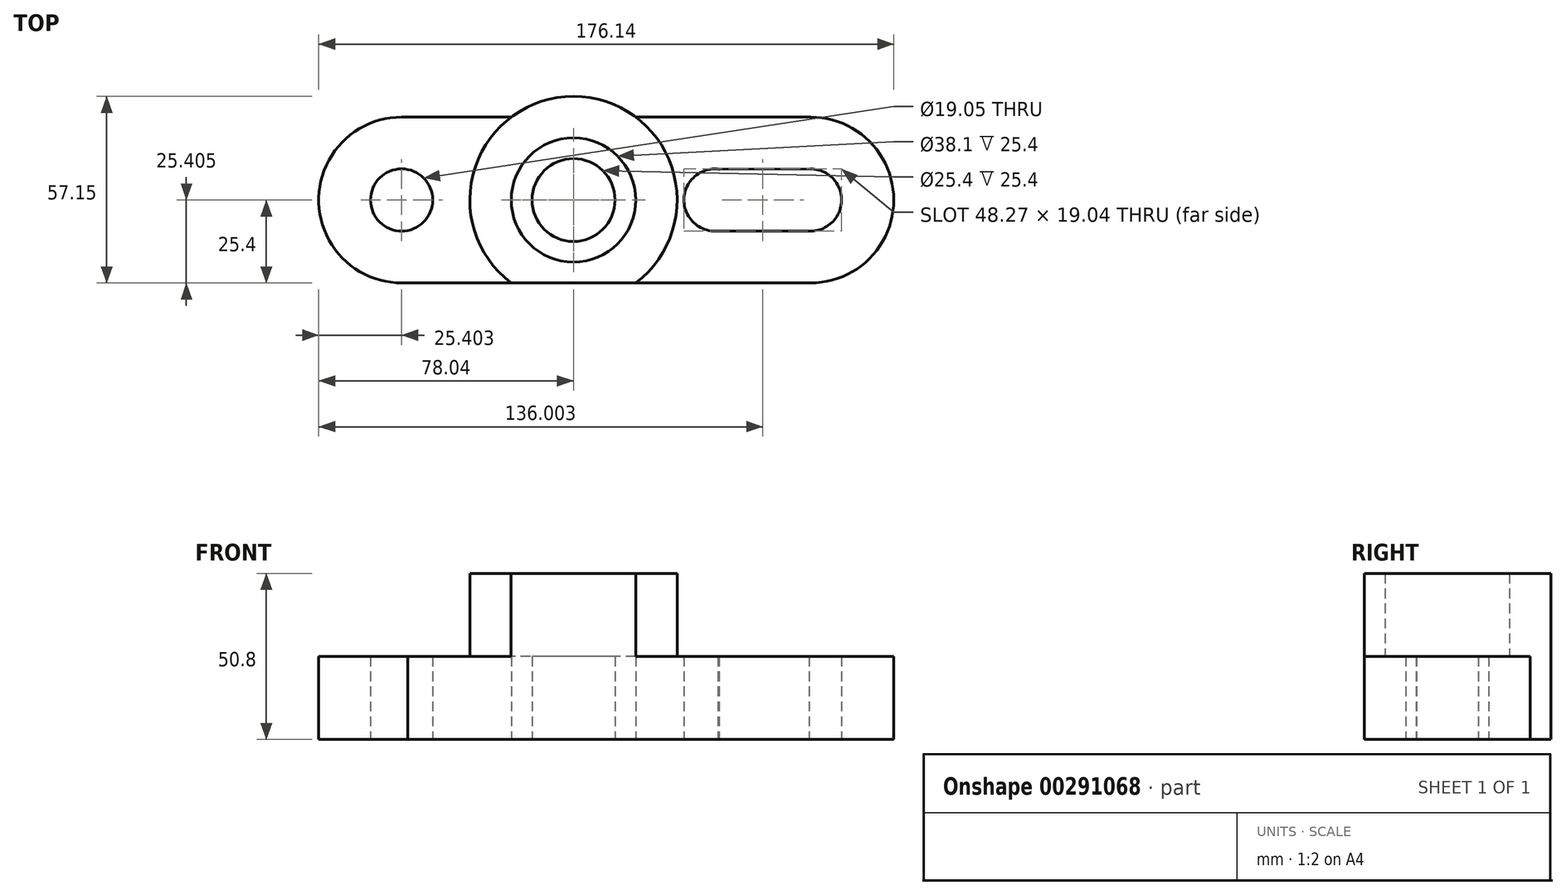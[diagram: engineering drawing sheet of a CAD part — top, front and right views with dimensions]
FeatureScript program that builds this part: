
annotation { "Feature Type Name" : "Feature", "Feature Type Description" : "" }
export const myFeature = defineFeature(function(context is Context, id is Id, definition is map)
    precondition{}
    {
        {
            var Q0;
            Q0=qCreatedBy(makeId("Top.planeOp"),FACE);
            var sketch = newSketch(context, id + "F0", { "sketchPlane" : qUnion([Q0])});
            skCircle(sketch, "E0", {"center": v(0, 0) * mm, "radius": 12.7 * mm});
            skCircle(sketch, "E1", {"center": v(0, 0) * mm, "radius": 19.05 * mm});
            skCircle(sketch, "E2", {"center": v(0, 0) * mm, "radius": 31.75 * mm});
            skArc(sketch, "E3", {"start": v(-52.64, 25.4) * mm, "mid": v(-78.02, -0.9) * mm, "end": v(-50.82, -25.33) * mm});
            skArc(sketch, "E4", {"start": v(72.69, -25.4) * mm, "mid": v(98.1, 0) * mm, "end": v(72.7, 25.4) * mm});
            skLineSegment(sketch, "E5", {"start": v(-54.48, -25.33) * mm, "end": v(72.69, -25.4) * mm});
            skLineSegment(sketch, "E6", {"start": v(72.7, 25.4) * mm, "end": v(-52.64, 25.4) * mm});
            skCircle(sketch, "E7", {"center": v(-52.64, 0) * mm, "radius": 9.53 * mm});
            skCircle(sketch, "E8", {"center": v(43.35, 0) * mm, "radius": 9.53 * mm});
            skCircle(sketch, "E9", {"center": v(72.57, 0) * mm, "radius": 9.53 * mm});
            skLineSegment(sketch, "E10", {"start": v(44.6, 9.44) * mm, "end": v(72.54, 9.52) * mm});
            skLineSegment(sketch, "E11", {"start": v(44.18, -9.49) * mm, "end": v(72.12, -9.51) * mm});
            skSolve(sketch);
        }
        {
            var Q0;
            {var subQ0=sQuery(id+"F0.wireOp",EDGE,"E6");var subQ1=sQuery(id+"F0.wireOp",EDGE,"E2");var subQ2=makeQuery(id+"F0.imprint","INTERSECT",VERTEX,{"disambiguationData":[OD(0.0)],"derivedFrom":[subQ1,subQ0]});Q0=makeQuery(id+"F0.imprint","IMPRINT",FACE,{"disambiguationData":[TD([[makeQuery(id+"F0.imprint","IMPRINT",EDGE,{"disambiguationData":[TD([[subQ2,1.0]])],"derivedFrom":subQ1}),1.0]])]});}
            var Q1;
            {var subQ0=sQuery(id+"F0.wireOp",EDGE,"E5");var subQ1=sQuery(id+"F0.wireOp",EDGE,"E2");var subQ2=makeQuery(id+"F0.imprint","INTERSECT",VERTEX,{"disambiguationData":[OD(0.0)],"derivedFrom":[subQ1,subQ0]});Q1=makeQuery(id+"F0.imprint","IMPRINT",FACE,{"disambiguationData":[TD([[makeQuery(id+"F0.imprint","IMPRINT",EDGE,{"disambiguationData":[TD([[subQ2,-1.0]])],"derivedFrom":subQ1}),1.0]])]});}
            var Q2;
            {var subQ0=sQuery(id+"F0.wireOp",EDGE,"E5");var subQ1=sQuery(id+"F0.wireOp",EDGE,"E3");var subQ2=makeQuery(id+"F0.imprint","INTERSECT",VERTEX,{"disambiguationData":[OD(0.0)],"derivedFrom":[subQ1,subQ0]});Q2=makeQuery(id+"F0.imprint","IMPRINT",FACE,{"disambiguationData":[TD([[makeQuery(id+"F0.imprint","IMPRINT",EDGE,{"disambiguationData":[TD([[subQ2,1.0]])],"derivedFrom":subQ1}),1.0]])]});}
            var Q3;
            Q3=makeQuery(id+"F0.imprint","IMPRINT",FACE,{"disambiguationData":[TD([[makeQuery(id+"F0.imprint","IMPRINT",EDGE,{"derivedFrom":sQuery(id+"F0.wireOp",EDGE,"E7")}),-1.0]])]});
            var Q4;
            {var subQ1=sQuery(id+"F0.wireOp",EDGE,"E4");Q4=makeQuery(id+"F0.imprint","IMPRINT",FACE,{"disambiguationData":[TD([[makeQuery(id+"F0.imprint","IMPRINT",EDGE,{"derivedFrom":subQ1}),1.0]])]});}
            var Q5;
            Q5=makeQuery(id+"F0.imprint","IMPRINT",FACE,{"disambiguationData":[TD([[makeQuery(id+"F0.imprint","IMPRINT",EDGE,{"derivedFrom":sQuery(id+"F0.wireOp",EDGE,"E1")}),-1.0]])]});
            extrude(context, id + "F1", {"entities" : qUnion([Q0, Q1, Q2, Q3, Q4, Q5]), "depth" : 25.4 * mm});
        }
        {
            var Q0;
            Q0=makeQuery(id+"F0.imprint","IMPRINT",FACE,{"disambiguationData":[TD([[makeQuery(id+"F0.imprint","IMPRINT",EDGE,{"derivedFrom":sQuery(id+"F0.wireOp",EDGE,"E1")}),-1.0]])]});
            var Q1;
            {var subQ0=sQuery(id+"F0.wireOp",EDGE,"E5");var subQ1=sQuery(id+"F0.wireOp",EDGE,"E2");var subQ2=makeQuery(id+"F0.imprint","INTERSECT",VERTEX,{"disambiguationData":[OD(0.0)],"derivedFrom":[subQ1,subQ0]});Q1=makeQuery(id+"F0.imprint","IMPRINT",FACE,{"disambiguationData":[TD([[makeQuery(id+"F0.imprint","IMPRINT",EDGE,{"disambiguationData":[TD([[subQ2,-1.0]])],"derivedFrom":subQ1}),1.0]])]});}
            var Q2;
            {var subQ0=sQuery(id+"F0.wireOp",EDGE,"E6");var subQ1=sQuery(id+"F0.wireOp",EDGE,"E2");var subQ2=makeQuery(id+"F0.imprint","INTERSECT",VERTEX,{"disambiguationData":[OD(0.0)],"derivedFrom":[subQ1,subQ0]});Q2=makeQuery(id+"F0.imprint","IMPRINT",FACE,{"disambiguationData":[TD([[makeQuery(id+"F0.imprint","IMPRINT",EDGE,{"disambiguationData":[TD([[subQ2,1.0]])],"derivedFrom":subQ1}),1.0]])]});}
            extrude(context, id + "F2", {"entities" : qUnion([Q0, Q1, Q2]), "operationType" : NewBodyOperationType.ADD, "depth" : 50.8 * mm});
        }
        {
            var Q0;
            Q0=makeQuery(id+"F0.imprint","IMPRINT",FACE,{"disambiguationData":[TD([[makeQuery(id+"F0.imprint","IMPRINT",EDGE,{"derivedFrom":sQuery(id+"F0.wireOp",EDGE,"E0")}),-1.0]])]});
            extrude(context, id + "F3", {"entities" : qUnion([Q0]), "operationType" : NewBodyOperationType.ADD, "depth" : 25.4 * mm});
        }
    });
